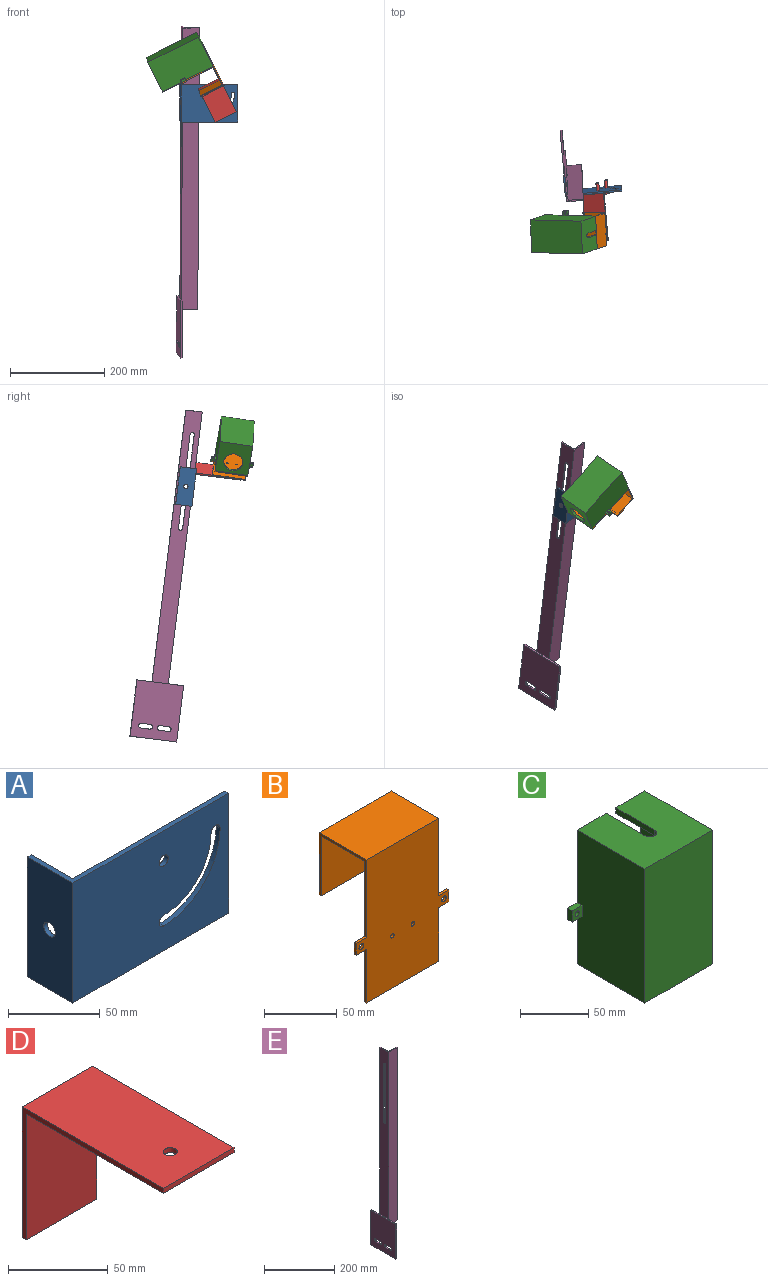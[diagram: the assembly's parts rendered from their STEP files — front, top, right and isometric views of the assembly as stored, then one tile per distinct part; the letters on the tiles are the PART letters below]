
ASSEMBLY  parts=5 mates=8
PART A: 14 faces, bbox 120x35x80 mm
  f0: plane 120x80mm, normal (0,-1,0), area 9083.2mm2, adj f2,f3,f6,f7,f9,f10,f11,f12
  f1: plane 117x80mm, normal (0,1,0), area 8843.2mm2, adj f3,f4,f6,f7,f9,f10,f11,f12
  f2: plane 80x35mm, normal (-1,0,0), area 2736.4mm2, adj f0,f5,f6,f7,f8
  f3: plane 80x3mm, normal (1,0,0), area 240mm2, adj f0,f1,f6,f7
  f4: plane 80x32mm, normal (1,0,0), area 2496.4mm2, adj f1,f5,f6,f7,f8
  f5: plane 80x3mm, normal (0,1,0), area 240mm2, adj f2,f4,f6,f7
  f6: plane 120x35mm, normal (0,0,1), area 456mm2, adj f0,f1,f2,f3,f4,f5
  f7: plane 120x35mm, normal (0,0,-1), area 456mm2, adj f0,f1,f2,f3,f4,f5
  f8: cylinder r=4.5mm len=9mm, axis (1,0,0), area 84.8mm2, adj f2,f4
  f9: cylinder r=3.5mm len=7mm, axis (0,-1,0), area 66mm2, adj f0,f1
  f10: cylinder r=36.5mm len=36.5mm, axis (0,-1,0), area 172mm2, adj f0,f1,f11,f13
  f11: cylinder r=3.5mm len=7mm, axis (0,-1,0), area 33mm2, adj f0,f1,f10,f12
  f12: cylinder r=43.5mm len=43.5mm, axis (0,-1,0), area 205mm2, adj f0,f1,f11,f13
  f13: cylinder r=3.5mm len=7mm, axis (0,-1,0), area 33mm2, adj f0,f1,f10,f12
PART B: 22 faces, bbox 90x46x120 mm
  f0: plane 10x2mm, normal (0,0,1), area 20mm2, adj f1,f14,f16,f17
  f1: plane 10x2mm, normal (-1,0,0), area 20mm2, adj f0,f2,f16,f17
  f2: plane 10x2mm, normal (0,0,-1), area 20mm2, adj f1,f3,f16,f17
  f3: plane 45x2mm, normal (-1,0,0), area 90mm2, adj f2,f4,f16,f17
  f4: plane 70x2mm, normal (0,0,-1), area 140mm2, adj f3,f5,f16,f17
  f5: plane 45x2mm, normal (1,0,0), area 90mm2, adj f4,f6,f16,f17
  f6: plane 10x2mm, normal (0,0,-1), area 20mm2, adj f5,f7,f16,f17
  f7: plane 10x2mm, normal (1,0,0), area 20mm2, adj f6,f8,f16,f17
  f8: plane 10x2mm, normal (0,0,1), area 20mm2, adj f7,f9,f16,f17
  f9: plane 65x46mm, normal (1,0,0), area 318mm2, adj f8,f10,f16,f17,f18,f19,f20,f21
  f10: plane 70x46mm, normal (0,0,1), area 3220mm2, adj f9,f14,f17,f21
  f11: cylinder r=1.75mm len=3.5mm, axis (0,-1,0), area 22mm2, adj f16,f17
  f12: cylinder r=2.25mm len=4.5mm, axis (0,-1,0), area 28.3mm2, adj f16,f17
  f13: cylinder r=2.25mm len=4.5mm, axis (0,-1,0), area 28.3mm2, adj f16,f17
  f14: plane 65x46mm, normal (-1,0,0), area 318mm2, adj f0,f10,f16,f17,f18,f19,f20,f21
  f15: cylinder r=1.75mm len=3.5mm, axis (0,-1,0), area 22mm2, adj f16,f17
  f16: plane 118x90mm, normal (0,1,0), area 8408.9mm2, adj f0,f1,f2,f3,f4,f5,f6,f7
  f17: plane 120x90mm, normal (0,-1,0), area 8548.9mm2, adj f0,f1,f2,f3,f4,f5,f6,f7
  f18: plane 70x42mm, normal (0,0,-1), area 2940mm2, adj f9,f14,f16,f19
  f19: plane 70x50mm, normal (0,-1,0), area 3500mm2, adj f9,f14,f18,f20
  f20: plane 70x2mm, normal (0,0,-1), area 140mm2, adj f9,f14,f19,f21
  f21: plane 70x52mm, normal (0,1,0), area 3640mm2, adj f9,f10,f14,f20
PART C: 25 faces, bbox 90x70x120 mm
  f0: plane 10x5mm, normal (0,0,-1), area 50mm2, adj f1,f4,f5,f13
  f1: plane 10x5mm, normal (-1,0,0), area 50mm2, adj f0,f3,f4,f5
  f2: cylinder r=2.25mm len=5mm, axis (0,1,0), area 70.7mm2, adj f4,f5
  f3: plane 10x5mm, normal (0,0,1), area 50mm2, adj f1,f4,f5,f13
  f4: plane 10x10mm, normal (0,-1,0), area 84.1mm2, adj f0,f1,f2,f3,f13
  f5: plane 120x90mm, normal (0,1,0), area 1918.2mm2, adj f0,f1,f2,f3,f6,f7,f8,f9
  f6: plane 10x5mm, normal (0,0,1), area 50mm2, adj f5,f7,f10,f11
  f7: plane 10x5mm, normal (1,0,0), area 50mm2, adj f5,f6,f9,f10
  f8: cylinder r=2.25mm len=5mm, axis (0,1,0), area 70.7mm2, adj f5,f10
  f9: plane 10x5mm, normal (0,0,-1), area 50mm2, adj f5,f7,f10,f11
  f10: plane 10x10mm, normal (0,-1,0), area 84.1mm2, adj f6,f7,f8,f9,f11
  f11: plane 120x70mm, normal (1,0,0), area 8350mm2, adj f5,f6,f9,f10,f12,f14,f15
  f12: plane 70x70mm, normal (0,0,1), area 4460.7mm2, adj f5,f11,f13,f15,f21,f22,f23
  f13: plane 120x70mm, normal (-1,0,0), area 8350mm2, adj f0,f3,f4,f5,f12,f14,f15
  f14: plane 70x70mm, normal (0,0,-1), area 3643.4mm2, adj f5,f11,f13,f15,f24
  f15: plane 120x70mm, normal (0,-1,0), area 8400mm2, adj f11,f12,f13,f14
  f16: plane 110x65mm, normal (1,0,0), area 7150mm2, adj f5,f17,f19,f20
  f17: plane 65x60mm, normal (0,0,1), area 2643.4mm2, adj f5,f16,f18,f20,f24
  f18: plane 110x65mm, normal (-1,0,0), area 7150mm2, adj f5,f17,f19,f20
  f19: plane 65x60mm, normal (0,0,-1), area 3460.7mm2, adj f5,f16,f18,f20,f21,f22,f23
  f20: plane 110x60mm, normal (0,1,0), area 6600mm2, adj f16,f17,f18,f19
  f21: plane 40x5mm, normal (1,0,0), area 200mm2, adj f5,f12,f19,f22
  f22: cylinder r=5mm len=10mm, axis (0,0,1), area 78.5mm2, adj f12,f19,f21,f23
  f23: plane 40x5mm, normal (-1,0,0), area 200mm2, adj f5,f12,f19,f22
  f24: cylinder r=20mm len=40mm, axis (0,0,-1), area 628.3mm2, adj f14,f17
PART D: 13 faces, bbox 50x120x80 mm
  f0: plane 50x3mm, normal (0,0,-1), area 150mm2, adj f1,f5,f6,f7
  f1: plane 80x50mm, normal (0,1,0), area 3943.5mm2, adj f0,f2,f6,f7,f9,f11
  f2: plane 100x50mm, normal (0,0,1), area 4961.5mm2, adj f1,f3,f6,f7,f8
  f3: plane 50x3mm, normal (0,-1,0), area 150mm2, adj f2,f4,f6,f7
  f4: plane 97x50mm, normal (0,0,-1), area 4811.5mm2, adj f3,f5,f6,f7,f8
  f5: plane 77x50mm, normal (0,-1,0), area 3850mm2, adj f0,f4,f6,f7
  f6: plane 100x80mm, normal (1,0,0), area 531mm2, adj f0,f1,f2,f3,f4,f5
  f7: plane 100x80mm, normal (-1,0,0), area 531mm2, adj f0,f1,f2,f3,f4,f5
  f8: cylinder r=3.5mm len=7mm, axis (0,0,1), area 66mm2, adj f2,f4
  f9: cylinder r=3mm len=20mm, axis (0,-1,0), area 377mm2, adj f1,f10
  f10: plane 6x6mm, normal (0,1,0), area 28.3mm2, adj f9
  f11: cylinder r=3mm len=20mm, axis (0,-1,0), area 377mm2, adj f1,f12
  f12: plane 6x6mm, normal (0,1,0), area 28.3mm2, adj f11
PART E: 26 faces, bbox 39x100x700 mm
  f0: plane 580x35mm, normal (-1,0,0), area 18436.4mm2, adj f2,f5,f6,f8,f9,f10,f11,f18
  f1: plane 600x32mm, normal (1,0,0), area 17336.4mm2, adj f4,f5,f6,f7,f8,f9,f10,f11
  f2: plane 600x35mm, normal (0,-1,0), area 21000mm2, adj f0,f3,f6,f7,f25
  f3: plane 600x3mm, normal (1,0,0), area 1800mm2, adj f2,f4,f6,f7
  f4: plane 600x32mm, normal (0,1,0), area 19200mm2, adj f1,f3,f6,f7
  f5: plane 600x3mm, normal (0,1,0), area 1800mm2, adj f0,f1,f6,f7,f25
  f6: plane 35x35mm, normal (0,0,1), area 201mm2, adj f0,f1,f2,f3,f4,f5
  f7: plane 35x35mm, normal (0,0,-1), area 201mm2, adj f1,f2,f3,f4,f5,f25
  f8: plane 200x3mm, normal (0,-1,0), area 600mm2, adj f0,f1,f9,f11
  f9: cylinder r=4.5mm len=9mm, axis (-1,0,0), area 42.4mm2, adj f0,f1,f8,f10
  f10: plane 200x3mm, normal (0,1,0), area 600mm2, adj f0,f1,f9,f11
  f11: cylinder r=4.5mm len=9mm, axis (-1,0,0), area 42.4mm2, adj f0,f1,f8,f10
  f12: cylinder r=5mm len=10mm, axis (1,0,0), area 62.8mm2, adj f13,f23,f24,f25
  f13: plane 20x4mm, normal (0,0,-1), area 80mm2, adj f12,f14,f24,f25
  f14: cylinder r=5mm len=10mm, axis (1,0,0), area 62.8mm2, adj f13,f23,f24,f25
  f15: plane 20x4mm, normal (0,0,1), area 80mm2, adj f16,f21,f24,f25
  f16: cylinder r=5mm len=10mm, axis (1,0,0), area 62.8mm2, adj f15,f17,f24,f25
  f17: plane 20x4mm, normal (0,0,-1), area 80mm2, adj f16,f21,f24,f25
  f18: plane 100x4mm, normal (0,0,1), area 400mm2, adj f0,f19,f22,f24,f25
  f19: plane 120x4mm, normal (0,1,0), area 480mm2, adj f18,f20,f24,f25
  f20: plane 100x4mm, normal (0,0,-1), area 400mm2, adj f19,f22,f24,f25
  f21: cylinder r=5mm len=10mm, axis (1,0,0), area 62.8mm2, adj f15,f17,f24,f25
  f22: plane 120x4mm, normal (0,-1,0), area 480mm2, adj f18,f20,f24,f25
  f23: plane 20x4mm, normal (0,0,1), area 80mm2, adj f12,f14,f24,f25
  f24: plane 120x100mm, normal (-1,0,0), area 11442.9mm2, adj f12,f13,f14,f15,f16,f17,f18,f19
  f25: plane 120x100mm, normal (1,0,0), area 10742.9mm2, adj f2,f5,f7,f12,f13,f14,f15,f16
PLACE A rot(axis=(0.81,0,0.59),8.8deg) t=(-193.88,-207.25,439.41)mm
PLACE B rot(axis=(-0.44,0.53,-0.73),100.2deg) t=(-236.47,-256.32,514.77)mm
PLACE C rot(axis=(-0.44,0.53,-0.73),100.2deg) t=(-267.64,-266.89,576.55)mm
PLACE D rot(axis=(0.29,-0.95,0.12),28.3deg) t=(-121.62,-200.64,439.46)mm
PLACE E rot(axis=(0.81,0,0.59),8.8deg) t=(-193.41,-154.8,43.68)mm
MATE planar A.f0 <-> D.f9  axis (0.09,-0.99,-0.12) through (-135.79,-206.94,479.61)mm
MATE planar B.f21 <-> D.f2  axis (0.45,0.15,-0.88) through (-151.93,-320.17,494.38)mm
MATE parallel B.f17 <-> C.f5  axis (-0.45,-0.15,0.88) through (-181.33,-292.33,536.42)mm
MATE cylindrical A.f9 <-> D.f9  axis (-0.09,0.99,0.12) through (-124.11,-205.35,499.72)mm
MATE fastened C.f8 <-> B.f12  axis (0.45,0.15,-0.88) through (-188.27,-331.63,526.2)mm
MATE planar A.f1 <-> E.f2  axis (-0.09,0.99,0.12) through (-132.46,-208.58,519.52)mm
MATE cylindrical C.f8 <-> B.f12  axis (0.45,0.15,-0.88) through (-190.49,-332.38,530.62)mm
MATE planar A.f4 <-> E.f0  axis (1,0.09,0.01) through (-192.4,-193.11,481.47)mm
